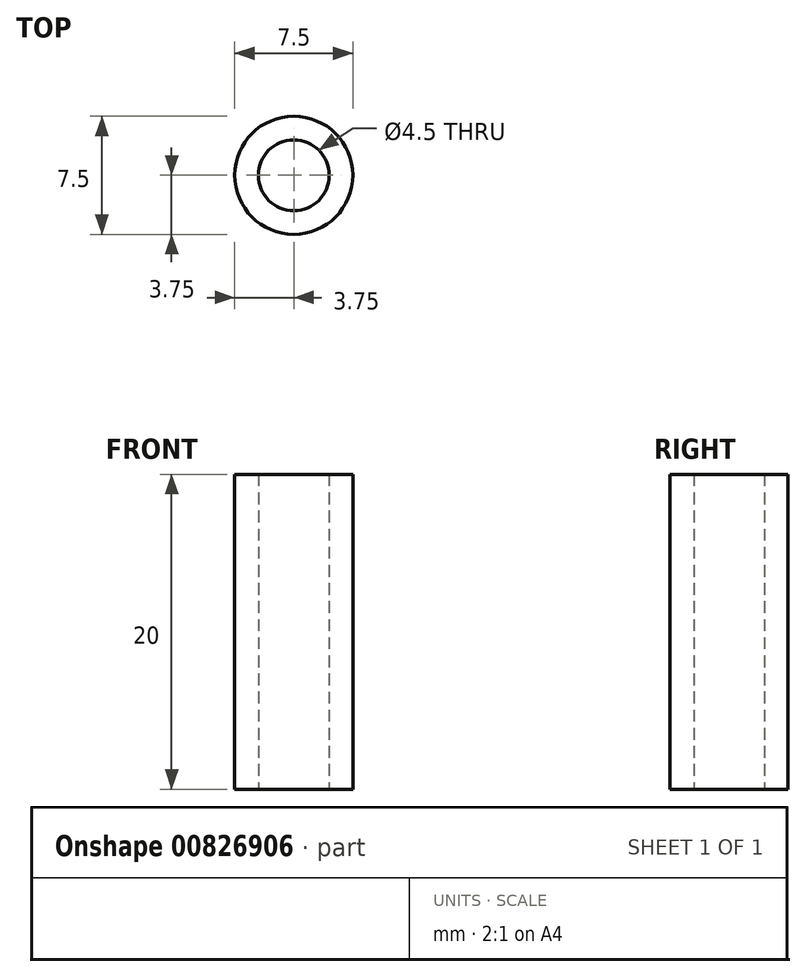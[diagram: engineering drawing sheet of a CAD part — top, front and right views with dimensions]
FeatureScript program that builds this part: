
annotation { "Feature Type Name" : "Feature", "Feature Type Description" : "" }
export const myFeature = defineFeature(function(context is Context, id is Id, definition is map)
    precondition{}
    {
        {
            var Q0;
            Q0=qCreatedBy(makeId("Top.planeOp"),FACE);
            var sketch = newSketch(context, id + "F0", { "sketchPlane" : qUnion([Q0])});
            skCircle(sketch, "E0", {"center": v(0, 0) * mm, "radius": 3.75 * mm});
            skCircle(sketch, "E1", {"center": v(0, 0) * mm, "radius": 2.25 * mm});
            skSolve(sketch);
        }
        {
            var Q0;
            Q0=makeQuery(id+"F0.imprint","IMPRINT",FACE,{"disambiguationData":[TD([[makeQuery(id+"F0.imprint","IMPRINT",EDGE,{"derivedFrom":sQuery(id+"F0.wireOp",EDGE,"E0")}),1.0]])]});
            extrude(context, id + "F1", {"entities" : qUnion([Q0]), "depth" : 20 * mm, "offsetDistance" : 25 * mm});
        }
    });
